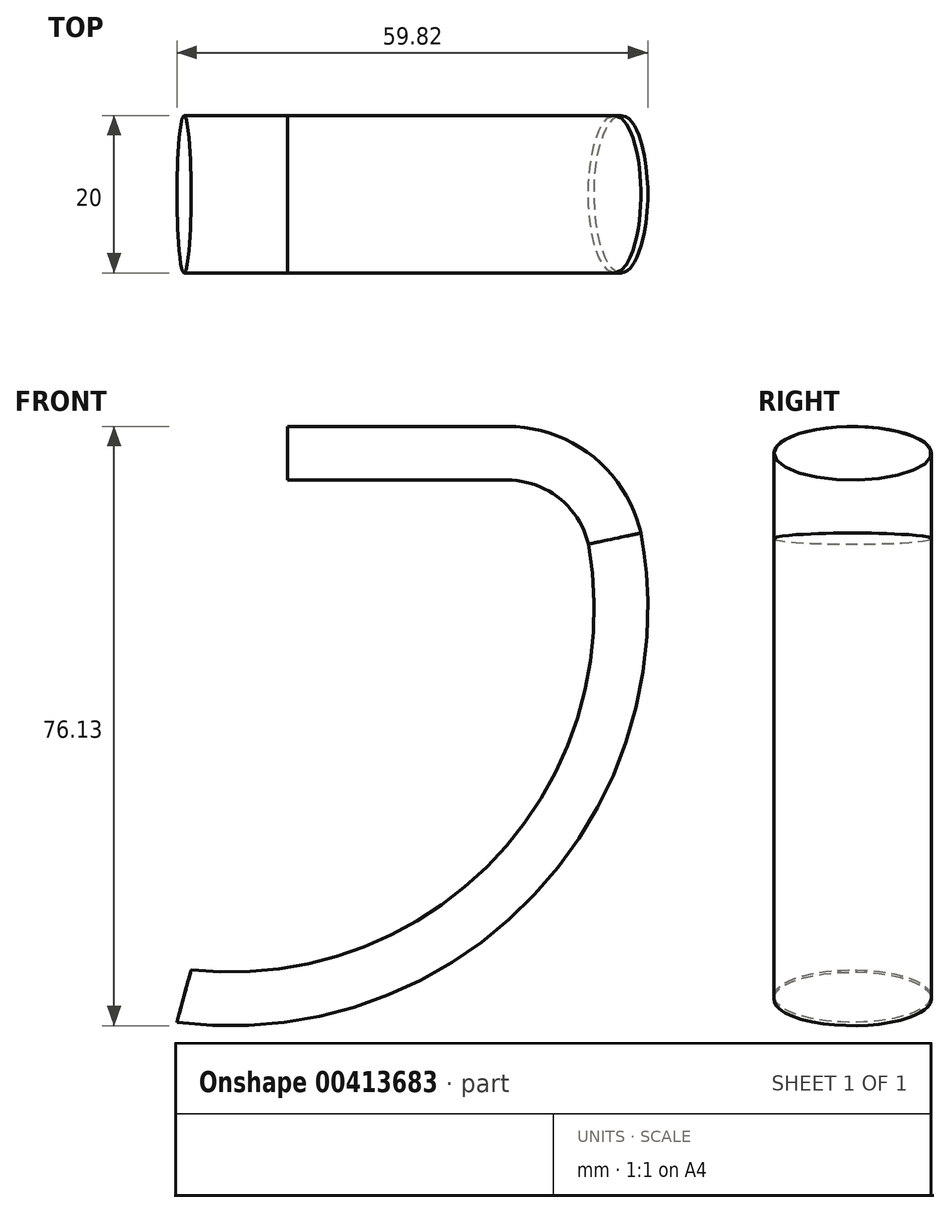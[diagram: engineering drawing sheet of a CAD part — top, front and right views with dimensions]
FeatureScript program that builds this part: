
annotation { "Feature Type Name" : "Feature", "Feature Type Description" : "" }
export const myFeature = defineFeature(function(context is Context, id is Id, definition is map)
    precondition{}
    {
        {
            var Q0;
            Q0=qCreatedBy(makeId("Front.planeOp"),FACE);
            var sketch = newSketch(context, id + "F0", { "sketchPlane" : qUnion([Q0])});
            skLineSegment(sketch, "E0", {"start": v(0, 60) * mm, "end": v(27.9, 60) * mm});
            skPoint(sketch, "E1.visualSharp", {"position": v(35, 60) * mm});
            skArc(sketch, "E1.filletArc", {"start": v(37.63, 52.32) * mm, "mid": v(34.1, 57.85) * mm, "end": v(27.9, 60) * mm});
            skPoint(sketch, "E2", {"position": v(-18.22, 0) * mm});
            skArc(sketch, "E3", {"start": v(-14.22, -0.81) * mm, "mid": v(25.41, 12.38) * mm, "end": v(37.63, 52.32) * mm});
            skSolve(sketch);
        }
        {
            var Q0;
            Q0=qCreatedBy(makeId("Right.planeOp"),FACE);
            var sketch = newSketch(context, id + "F1", { "sketchPlane" : qUnion([Q0])});
            skEllipse(sketch, "E4", {"center": v(0, 63.98) * mm, "majorRadius": 10 * mm, "minorRadius": 3.4 * mm, "majorAxis": v(-1, 0)});
            skSolve(sketch);
        }
        {
            var Q0;
            Q0=makeQuery(id+"F1.imprint","IMPRINT",FACE,{"disambiguationData":[TD([[makeQuery(id+"F1.imprint","IMPRINT",EDGE,{"derivedFrom":sQuery(id+"F1.wireOp",EDGE,"E4")}),1.0]])]});
            var Q1;
            Q1=sQuery(id+"F0.wireOp",EDGE,"E0");
            var Q2;
            Q2=sQuery(id+"F0.wireOp",EDGE,"E1.filletArc");
            var Q3;
            Q3=sQuery(id+"F0.wireOp",EDGE,"E3");
            sweep(context, id + "F2", {"profiles" : qUnion([Q0]), "path" : qUnion([Q1, Q2, Q3])});
        }
        {
            var Q0;
            Q0=qCreatedBy(makeId("Front.planeOp"),FACE);
            var sketch = newSketch(context, id + "F3", { "sketchPlane" : qUnion([Q0])});
            skLineSegment(sketch, "E5", {"start": v(-14.93, -11.44) * mm, "end": v(-10.82, 3.64) * mm});
            skLineSegment(sketch, "E6", {"start": v(-10.82, 3.64) * mm, "end": v(-21.16, 0.81) * mm});
            skLineSegment(sketch, "E7", {"start": v(-21.16, 0.81) * mm, "end": v(-14.93, -11.44) * mm});
            skSolve(sketch);
        }
        {
            var Q0;
            Q0=makeQuery(id+"F3.imprint","IMPRINT",FACE,{"disambiguationData":[TD([[makeQuery(id+"F3.imprint","IMPRINT",EDGE,{"derivedFrom":sQuery(id+"F3.wireOp",EDGE,"E5")}),1.0]])]});
            extrude(context, id + "F4", {"entities" : qUnion([Q0]), "operationType" : NewBodyOperationType.REMOVE, "oppositeDirection" : true, "depth" : 25 * mm, "symmetric" : true});
        }
    });
